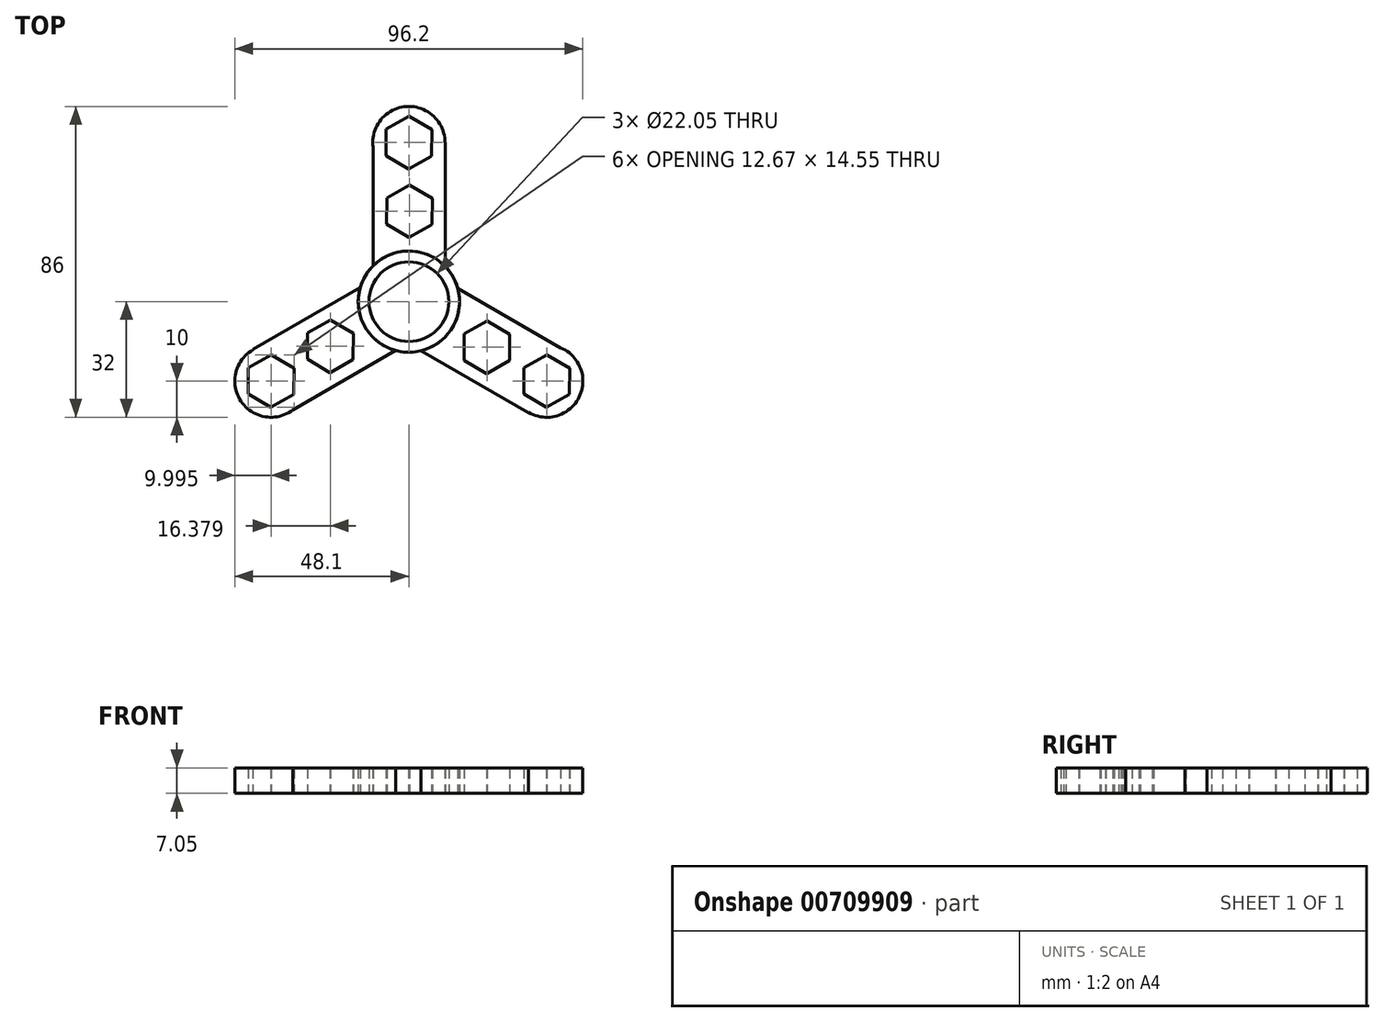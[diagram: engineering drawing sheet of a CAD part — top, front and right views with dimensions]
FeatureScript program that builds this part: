
annotation { "Feature Type Name" : "Feature", "Feature Type Description" : "" }
export const myFeature = defineFeature(function(context is Context, id is Id, definition is map)
    precondition{}
    {
        {
            var Q0;
            Q0=qCreatedBy(makeId("Top.planeOp"),FACE);
            var sketch = newSketch(context, id + "F0", { "sketchPlane" : qUnion([Q0])});
            skCircle(sketch, "E0", {"center": v(0, 0) * mm, "radius": 11.03 * mm});
            skCircle(sketch, "E1", {"center": v(0, 0) * mm, "radius": 14 * mm});
            skLineSegment(sketch, "E2.bottom", {"start": v(-9.92, 44) * mm, "end": v(10.08, 44) * mm});
            skLineSegment(sketch, "E2.top", {"start": v(-9.92, 9) * mm, "end": v(10.08, 9) * mm});
            skLineSegment(sketch, "E2.left", {"start": v(-9.92, 44) * mm, "end": v(-9.92, 9) * mm});
            skLineSegment(sketch, "E2.right", {"start": v(10.08, 44) * mm, "end": v(10.08, 9) * mm});
            skCircle(sketch, "E3", {"center": v(0, 44) * mm, "radius": 10 * mm});
            skCircle(sketch, "E4.cCircle", {"center": v(0, 44) * mm, "radius": 6.3 * mm, "construction": true});
            skLineSegment(sketch, "E4.0", {"start": v(6.26, 40.3) * mm, "end": v(-0.07, 36.73) * mm});
            skLineSegment(sketch, "E4.1", {"start": v(-0.07, 36.73) * mm, "end": v(-6.33, 40.42) * mm});
            skLineSegment(sketch, "E4.2", {"start": v(-6.33, 40.42) * mm, "end": v(-6.26, 47.7) * mm});
            skLineSegment(sketch, "E4.3", {"start": v(-6.26, 47.7) * mm, "end": v(0.07, 51.27) * mm});
            skLineSegment(sketch, "E4.4", {"start": v(0.07, 51.27) * mm, "end": v(6.33, 47.58) * mm});
            skLineSegment(sketch, "E4.5", {"start": v(6.33, 47.58) * mm, "end": v(6.26, 40.3) * mm});
            skPoint(sketch, "E4.0.midPoint", {"position": v(3.1, 38.51) * mm});
            skCircle(sketch, "E5.cCircle", {"center": v(0.15, 25) * mm, "radius": 6.3 * mm, "construction": true});
            skLineSegment(sketch, "E5.0", {"start": v(6.42, 21.3) * mm, "end": v(0.08, 17.73) * mm});
            skLineSegment(sketch, "E5.1", {"start": v(0.08, 17.73) * mm, "end": v(-6.18, 21.42) * mm});
            skLineSegment(sketch, "E5.2", {"start": v(-6.18, 21.42) * mm, "end": v(-6.11, 28.7) * mm});
            skLineSegment(sketch, "E5.3", {"start": v(-6.11, 28.7) * mm, "end": v(0.22, 32.27) * mm});
            skLineSegment(sketch, "E5.4", {"start": v(0.22, 32.27) * mm, "end": v(6.49, 28.58) * mm});
            skLineSegment(sketch, "E5.5", {"start": v(6.49, 28.58) * mm, "end": v(6.42, 21.3) * mm});
            skPoint(sketch, "E5.0.midPoint", {"position": v(3.25, 19.51) * mm});
            skSolve(sketch);
        }
        {
            var Q0;
            {var subQ6=sQuery(id+"F0.wireOp",EDGE,"E4.3");Q0=makeQuery(id+"F0.imprint","IMPRINT",FACE,{"disambiguationData":[TD([[makeQuery(id+"F0.imprint","IMPRINT",EDGE,{"derivedFrom":subQ6}),1.0]])]});}
            var Q1;
            {var subQ10=sQuery(id+"F0.wireOp",EDGE,"E4.0");Q1=makeQuery(id+"F0.imprint","IMPRINT",FACE,{"disambiguationData":[TD([[makeQuery(id+"F0.imprint","IMPRINT",EDGE,{"derivedFrom":subQ10}),1.0]])]});}
            var Q2;
            Q2=makeQuery(id+"F0.imprint","IMPRINT",FACE,{"disambiguationData":[TD([[makeQuery(id+"F0.imprint","IMPRINT",EDGE,{"derivedFrom":sQuery(id+"F0.wireOp",EDGE,"E5.0")}),1.0]])]});
            var Q3;
            {var subQ1=sQuery(id+"F0.wireOp",EDGE,"E2.top");var subQ3=sQuery(id+"F0.wireOp",EDGE,"E0");var subQ4=makeQuery(id+"F0.imprint","INTERSECT",VERTEX,{"disambiguationData":[OD(0.0)],"derivedFrom":[subQ3,subQ1]});Q3=makeQuery(id+"F0.imprint","IMPRINT",FACE,{"disambiguationData":[TD([[makeQuery(id+"F0.imprint","IMPRINT",EDGE,{"disambiguationData":[TD([[subQ4,1.0]])],"derivedFrom":subQ3}),-1.0]])]});}
            var Q4;
            {var subQ1=sQuery(id+"F0.wireOp",EDGE,"E2.top");var subQ3=sQuery(id+"F0.wireOp",EDGE,"E0");var subQ7=makeQuery(id+"F0.imprint","INTERSECT",VERTEX,{"disambiguationData":[OD(0.0)],"derivedFrom":[subQ3,subQ1]});Q4=makeQuery(id+"F0.imprint","IMPRINT",FACE,{"disambiguationData":[TD([[makeQuery(id+"F0.imprint","IMPRINT",EDGE,{"disambiguationData":[TD([[subQ7,-1.0]])],"derivedFrom":subQ3}),-1.0]])]});}
            extrude(context, id + "F1", {"entities" : qUnion([Q0, Q1, Q2, Q3, Q4]), "depth" : 7.05 * mm, "offsetDistance" : 25 * mm});
        }
        {
            var Q0;
            Q0=makeQuery(id+"F1.opExtrude","SWEPT_BODY",BODY,{"disambiguationData":[OSD([sQuery(id+"F0.wireOp",EDGE,"E0"),sQuery(id+"F0.wireOp",EDGE,"E1"),sQuery(id+"F0.wireOp",EDGE,"E2.bottom"),sQuery(id+"F0.wireOp",EDGE,"E2.left"),sQuery(id+"F0.wireOp",EDGE,"E2.right"),sQuery(id+"F0.wireOp",EDGE,"E3"),sQuery(id+"F0.wireOp",EDGE,"E4.0"),sQuery(id+"F0.wireOp",EDGE,"E4.1"),sQuery(id+"F0.wireOp",EDGE,"E4.2"),sQuery(id+"F0.wireOp",EDGE,"E4.3"),sQuery(id+"F0.wireOp",EDGE,"E4.4"),sQuery(id+"F0.wireOp",EDGE,"E4.5"),sQuery(id+"F0.wireOp",EDGE,"E5.0"),sQuery(id+"F0.wireOp",EDGE,"E5.1"),sQuery(id+"F0.wireOp",EDGE,"E5.2"),sQuery(id+"F0.wireOp",EDGE,"E5.3"),sQuery(id+"F0.wireOp",EDGE,"E5.4"),sQuery(id+"F0.wireOp",EDGE,"E5.5")])]});
            var Q1;
            Q1=makeQuery(id+"F1.opExtrude","SWEPT_FACE",FACE,{"disambiguationData":[OSD([sQuery(id+"F0.wireOp",EDGE,"E1")])]});
            circularPattern(context, id + "F2", {"entities" : qUnion([Q0]), "axis" : qUnion([Q1]), "angle" : 360 * degree, "instanceCount" : 3, "equalSpace" : true});
        }
    });
